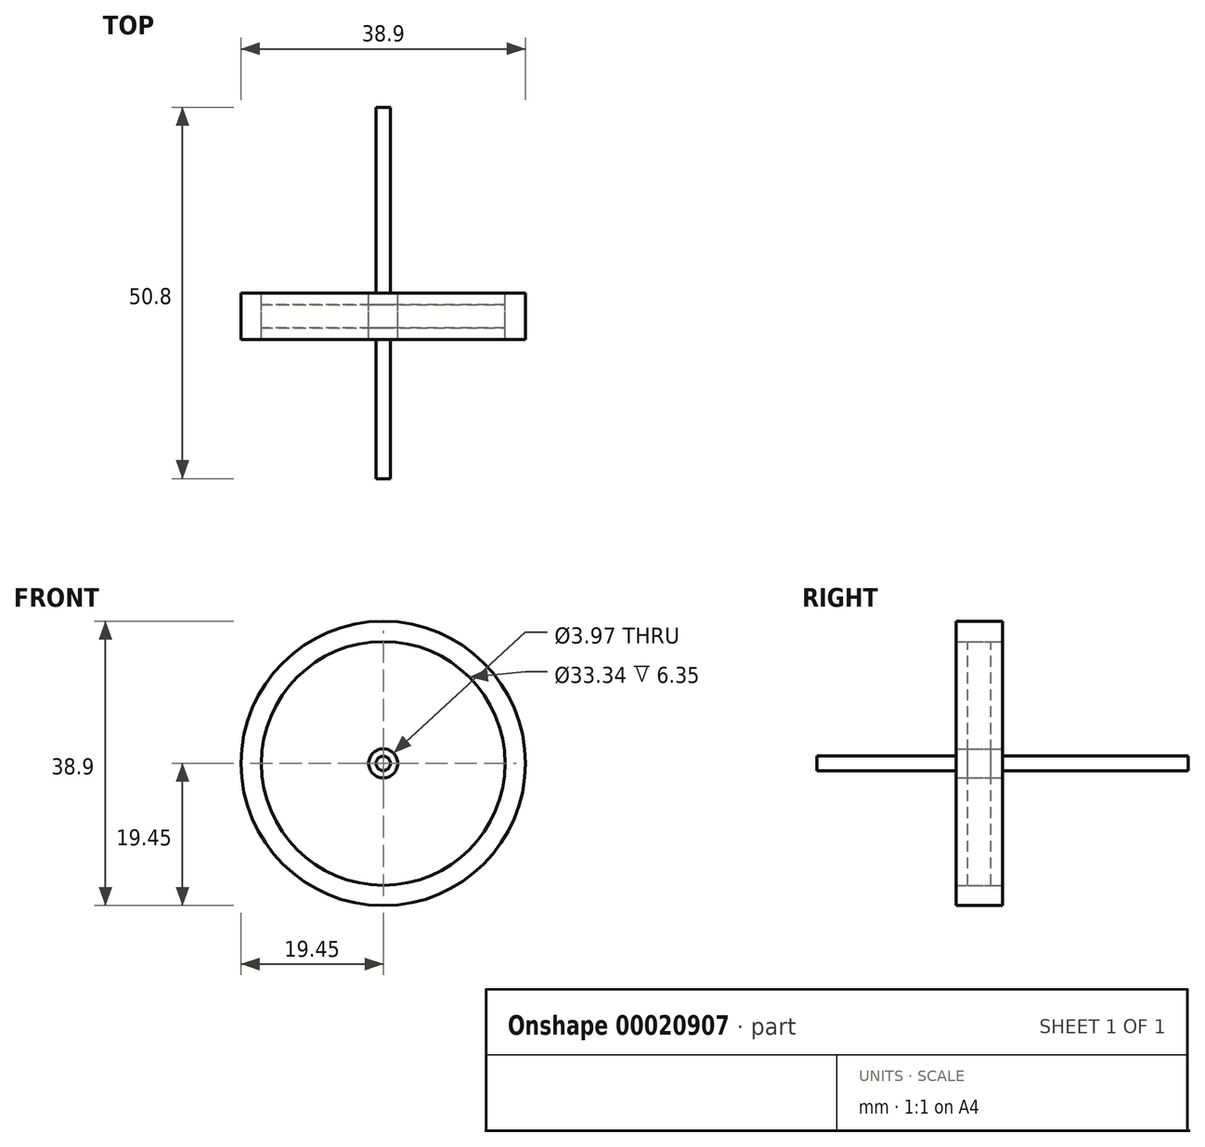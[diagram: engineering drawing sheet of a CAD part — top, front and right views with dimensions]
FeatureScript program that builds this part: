
annotation { "Feature Type Name" : "Feature", "Feature Type Description" : "" }
export const myFeature = defineFeature(function(context is Context, id is Id, definition is map)
    precondition{}
    {
        {
            var Q0;
            Q0=qCreatedBy(makeId("Front.planeOp"),FACE);
            var sketch = newSketch(context, id + "F0", { "sketchPlane" : qUnion([Q0])});
            skCircle(sketch, "E0", {"center": v(0, 0) * mm, "radius": 19.45 * mm});
            skCircle(sketch, "E1", {"center": v(0, 0) * mm, "radius": 1 * mm});
            skCircle(sketch, "E2", {"center": v(0, 0) * mm, "radius": 1.98 * mm});
            skCircle(sketch, "E3", {"center": v(0, 0) * mm, "radius": 16.67 * mm});
            skSolve(sketch);
        }
        {
            var Q0;
            Q0=makeQuery(id+"F0.imprint","IMPRINT",FACE,{"disambiguationData":[TD([[makeQuery(id+"F0.imprint","IMPRINT",EDGE,{"derivedFrom":sQuery(id+"F0.wireOp",EDGE,"E0")}),1.0]])]});
            extrude(context, id + "F1", {"entities" : qUnion([Q0]), "depth" : 6.35 * mm});
        }
        {
            var Q0;
            Q0=makeQuery(id+"F0.imprint","IMPRINT",FACE,{"disambiguationData":[TD([[makeQuery(id+"F0.imprint","IMPRINT",EDGE,{"derivedFrom":sQuery(id+"F0.wireOp",EDGE,"E1")}),-1.0]])]});
            extrude(context, id + "F2", {"entities" : qUnion([Q0]), "depth" : 6.35 * mm});
        }
        {
            var Q0;
            Q0=makeQuery(id+"F0.imprint","IMPRINT",FACE,{"disambiguationData":[TD([[makeQuery(id+"F0.imprint","IMPRINT",EDGE,{"derivedFrom":sQuery(id+"F0.wireOp",EDGE,"E2")}),-1.0]])]});
            extrude(context, id + "F3", {"entities" : qUnion([Q0]), "depth" : 4.76 * mm, "hasSecondDirection" : true, "secondDirectionOppositeDirection" : false, "secondDirectionDepth" : 1.59 * mm});
        }
        {
            var Q0;
            Q0=makeQuery(id+"F0.imprint","IMPRINT",FACE,{"disambiguationData":[TD([[makeQuery(id+"F0.imprint","IMPRINT",EDGE,{"derivedFrom":sQuery(id+"F0.wireOp",EDGE,"E1")}),1.0]])]});
            extrude(context, id + "F4", {"entities" : qUnion([Q0]), "operationType" : NewBodyOperationType.ADD, "depth" : 25.4 * mm, "hasSecondDirection" : true, "secondDirectionOppositeDirection" : true, "secondDirectionDepth" : 25.4 * mm});
        }
    });
